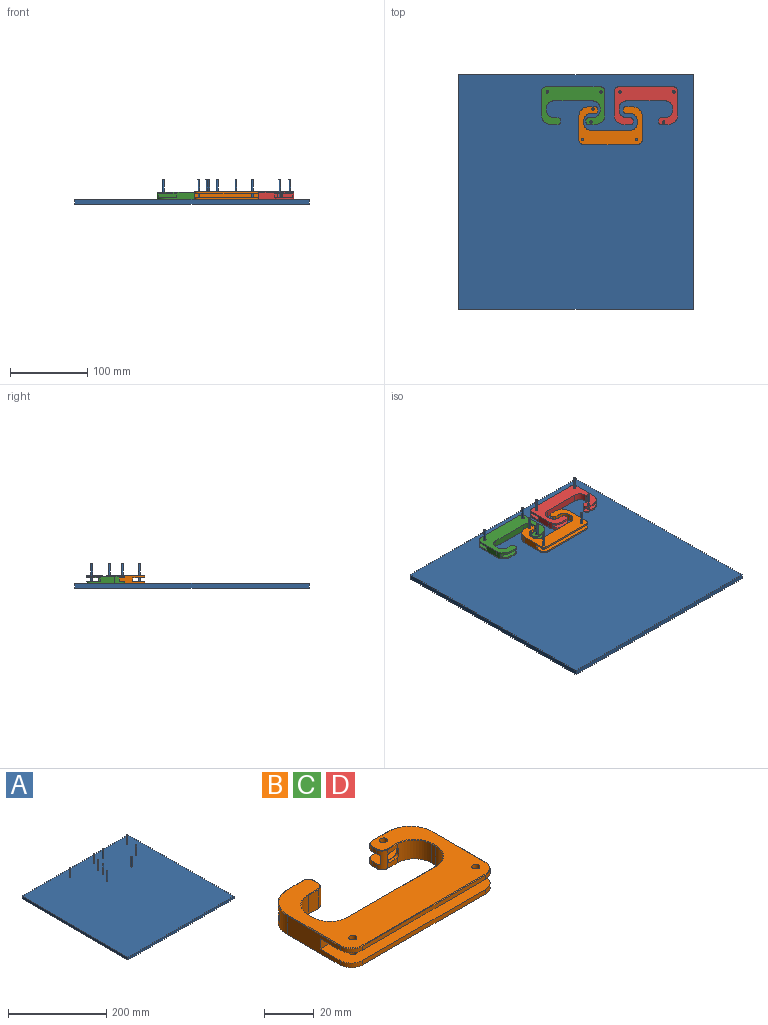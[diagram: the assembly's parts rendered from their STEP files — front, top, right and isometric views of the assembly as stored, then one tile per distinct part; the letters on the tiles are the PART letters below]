
ASSEMBLY  parts=4 mates=9
PART A: 24 faces, bbox 304.8x304.8x31.8 mm
  f0: plane 304.8x6.35mm, normal (1,0,0), area 1935.5mm2, adj f1,f3,f4,f5
  f1: plane 304.8x6.35mm, normal (0,1,0), area 1935.5mm2, adj f0,f2,f4,f5
  f2: plane 304.8x6.35mm, normal (-1,0,0), area 1935.5mm2, adj f1,f3,f4,f5
  f3: plane 304.8x6.35mm, normal (0,-1,0), area 1935.5mm2, adj f0,f2,f4,f5
  f4: plane 304.8x304.8mm, normal (0,0,1), area 92857.4mm2, adj f0,f1,f2,f3,f6,f8,f10,f12
  f5: plane 304.8x304.8mm, normal (0,0,-1), area 92903mm2, adj f0,f1,f2,f3
  f6: cylinder r=1.27mm len=25.4mm, axis (0,0,-1), area 202.7mm2, adj f4,f7
  f7: plane 2.54x2.54mm, normal (0,0,1), area 5.1mm2, adj f6
  f8: cylinder r=1.27mm len=25.4mm, axis (0,0,-1), area 202.7mm2, adj f4,f9
  f9: plane 2.54x2.54mm, normal (0,0,1), area 5.1mm2, adj f8
  f10: cylinder r=1.27mm len=25.4mm, axis (0,0,-1), area 202.7mm2, adj f4,f11
  f11: plane 2.54x2.54mm, normal (0,0,1), area 5.1mm2, adj f10
  f12: cylinder r=1.27mm len=25.4mm, axis (0,0,-1), area 202.7mm2, adj f4,f13
  f13: plane 2.54x2.54mm, normal (0,0,1), area 5.1mm2, adj f12
  f14: cylinder r=1.27mm len=25.4mm, axis (0,0,-1), area 202.7mm2, adj f4,f15
  f15: plane 2.54x2.54mm, normal (0,0,1), area 5.1mm2, adj f14
  f16: cylinder r=1.27mm len=25.4mm, axis (0,0,-1), area 202.7mm2, adj f4,f17
  f17: plane 2.54x2.54mm, normal (0,0,1), area 5.1mm2, adj f16
  f18: cylinder r=1.27mm len=25.4mm, axis (0,0,-1), area 202.7mm2, adj f4,f19
  f19: plane 2.54x2.54mm, normal (0,0,1), area 5.1mm2, adj f18
  f20: cylinder r=1.27mm len=25.4mm, axis (0,0,-1), area 202.7mm2, adj f4,f21
  f21: plane 2.54x2.54mm, normal (0,0,1), area 5.1mm2, adj f20
  f22: cylinder r=1.27mm len=25.4mm, axis (0,0,-1), area 202.7mm2, adj f4,f23
  f23: plane 2.54x2.54mm, normal (0,0,1), area 5.1mm2, adj f22
PART B: 87 faces, bbox 82.6x49.1x9.5 mm
  f0: plane 30.01x9.27mm, normal (-1,0,0), area 221.4mm2, adj f4,f17,f18,f42,f49,f73,f74,f86
  f1: plane 5.46x3.51mm, normal (0,-1,0), area 13.4mm2, adj f25,f27,f42,f76,f77,f78
  f2: plane 23.05x4.84mm, normal (0,1,0), area 82.7mm2, adj f21,f25,f46,f47,f75,f76,f77,f78
  f3: plane 69.85x2.24mm, normal (0,-1,0), area 156.6mm2, adj f18,f20,f42,f74
  f4: cylinder r=6.35mm len=6.35mm, axis (0,0,-1), area 19.8mm2, adj f0,f19,f51,f73
  f5: cylinder r=6.35mm len=6.35mm, axis (0,0,-1), area 19.8mm2, adj f6,f19,f55,f73
  f6: plane 30.01x9.27mm, normal (1,0,0), area 233.4mm2, adj f5,f20,f21,f42,f57,f72,f73,f74
  f7: cylinder r=1.63mm len=3.25mm, axis (0,0,-1), area 22.9mm2, adj f41,f73
  f8: cylinder r=1.63mm len=3.25mm, axis (0,0,-1), area 22.9mm2, adj f41,f73
  f9: plane 8.89x2.34mm, normal (0,1,0), area 20.8mm2, adj f15,f17,f42,f44
  f10: plane 8.89x2.09mm, normal (0,1,0), area 18.6mm2, adj f21,f23,f46,f61
  f11: cylinder r=3.17mm len=3.18mm, axis (0,0,-1), area 11.7mm2, adj f12,f22,f42,f47
  f12: plane 2.37x2.34mm, normal (-1,0,0), area 5.5mm2, adj f11,f25,f42,f47
  f13: plane 2.37x2.34mm, normal (1,0,0), area 5.5mm2, adj f15,f35,f42,f44
  f14: cylinder r=1.63mm len=3.25mm, axis (0,0,-1), area 23.9mm2, adj f42,f47
  f15: cylinder r=3.17mm len=3.18mm, axis (0,0,-1), area 11.7mm2, adj f9,f13,f42,f44
  f16: plane 8.89x2.09mm, normal (0,1,0), area 18.6mm2, adj f17,f39,f43,f50
  f17: cylinder r=12.7mm len=12.7mm, axis (0,0,-1), area 116.1mm2, adj f0,f9,f16,f42,f43,f44,f45,f48
  f18: cylinder r=6.35mm len=6.35mm, axis (0,0,-1), area 22.4mm2, adj f0,f3,f42,f74
  f19: plane 69.85x1.99mm, normal (0,-1,0), area 138.8mm2, adj f4,f5,f53,f73
  f20: cylinder r=6.35mm len=6.35mm, axis (0,0,-1), area 22.4mm2, adj f3,f6,f42,f74
  f21: cylinder r=12.7mm len=12.7mm, axis (0,0,-1), area 116.1mm2, adj f2,f6,f10,f22,f42,f46,f47,f59
  f22: plane 8.89x2.34mm, normal (0,1,0), area 20.8mm2, adj f11,f21,f42,f47
  f23: cylinder r=3.17mm len=3.18mm, axis (0,0,-1), area 10.4mm2, adj f10,f24,f46,f63
  f24: plane 2.37x2.09mm, normal (-1,0,0), area 4.9mm2, adj f23,f25,f46,f65
  f25: cylinder r=3.17mm len=9.27mm, axis (0,0,-1), area 37.8mm2, adj f1,f2,f12,f24,f26,f42,f46,f47
  f26: plane 5.46x3.26mm, normal (0,-1,0), area 12mm2, adj f25,f27,f69,f80,f81,f82
  f27: cylinder r=9.78mm len=9.78mm, axis (0,0,-1), area 138.9mm2, adj f1,f26,f28,f42,f71,f75,f76,f82
  f28: plane 9.27x2.37mm, normal (-1,0,0), area 22mm2, adj f27,f29,f42,f70
  f29: cylinder r=9.78mm len=9.78mm, axis (0,0,-1), area 142.4mm2, adj f28,f30,f42,f68
  f30: plane 50.29x9.27mm, normal (0,1,0), area 466.3mm2, adj f29,f31,f42,f66
  f31: cylinder r=9.78mm len=9.78mm, axis (0,0,-1), area 142.4mm2, adj f30,f32,f42,f64
  f32: plane 9.27x2.37mm, normal (1,0,0), area 22mm2, adj f31,f33,f42,f62
  f33: cylinder r=9.78mm len=9.78mm, axis (0,0,-1), area 142.4mm2, adj f32,f34,f42,f60
  f34: plane 9.27x5.46mm, normal (0,-1,0), area 50.6mm2, adj f33,f35,f42,f58
  f35: cylinder r=3.17mm len=9.27mm, axis (0,0,-1), area 38mm2, adj f13,f34,f36,f42,f43,f44,f45,f56
  f36: plane 2.37x2.09mm, normal (1,0,0), area 4.9mm2, adj f35,f39,f43,f54
  f37: cylinder r=1.63mm len=3.25mm, axis (0,0,-1), area 23.9mm2, adj f41,f46
  f38: cylinder r=1.63mm len=3.25mm, axis (0,0,-1), area 22.9mm2, adj f42,f74
  f39: cylinder r=3.17mm len=3.18mm, axis (0,0,-1), area 10.4mm2, adj f16,f36,f43,f52
  f40: cylinder r=1.63mm len=3.25mm, axis (0,0,-1), area 22.9mm2, adj f42,f74
  f41: plane 82.04x48.55mm, normal (0,0,1), area 2101.3mm2, adj f7,f8,f37,f48,f49,f50,f51,f52
  f42: plane 82.55x49.06mm, normal (0,0,-1), area 2192.5mm2, adj f0,f1,f3,f6,f9,f11,f12,f13
  f43: plane 23.5x7.17mm, normal (0,0,-1), area 142.8mm2, adj f16,f17,f35,f36,f39,f45
  f44: plane 23.5x7.17mm, normal (0,0,1), area 142.8mm2, adj f9,f13,f15,f17,f35,f45
  f45: plane 23.05x4.84mm, normal (0,1,0), area 111.5mm2, adj f17,f35,f43,f44
  f46: plane 23.5x7.17mm, normal (0,0,-1), area 134.5mm2, adj f2,f10,f21,f23,f24,f25,f37
  f47: plane 23.5x7.17mm, normal (0,0,1), area 134.5mm2, adj f2,f11,f12,f14,f21,f22,f25
  f48: cone r=12.45mm half-angle=45deg, axis (0,0,-1), area 7.1mm2, adj f17,f41,f49,f50
  f49: plane 30.01x0.25mm, normal (-0.71,0,0.71), area 10.8mm2, adj f0,f41,f48,f51
  f50: plane 8.89x0.25mm, normal (0,0.71,0.71), area 3.2mm2, adj f16,f41,f48,f52
  f51: cone r=6.1mm half-angle=45deg, axis (0,0,-1), area 3.5mm2, adj f4,f41,f49,f53
  f52: cone r=2.92mm half-angle=45deg, axis (0,0,-1), area 1.7mm2, adj f39,f41,f50,f54
  f53: plane 69.85x0.25mm, normal (0,-0.71,0.71), area 25.1mm2, adj f19,f41,f51,f55
  f54: plane 2.37x0.25mm, normal (0.71,0,0.71), area 0.9mm2, adj f36,f41,f52,f56
  f55: cone r=6.1mm half-angle=45deg, axis (0,0,-1), area 3.5mm2, adj f5,f41,f53,f57
  f56: cone r=2.92mm half-angle=45deg, axis (0,0,-1), area 1.7mm2, adj f35,f41,f54,f58
  f57: plane 30.01x0.25mm, normal (0.71,0,0.71), area 10.8mm2, adj f6,f41,f55,f59
  f58: plane 5.46x0.25mm, normal (0,-0.71,0.71), area 2mm2, adj f34,f41,f56,f60
  f59: cone r=12.45mm half-angle=45deg, axis (0,0,-1), area 7.1mm2, adj f21,f41,f57,f61
  f60: cone r=9.78mm half-angle=45deg, axis (0,0,1), area 5.6mm2, adj f33,f41,f58,f62
  f61: plane 8.89x0.25mm, normal (0,0.71,0.71), area 3.2mm2, adj f10,f41,f59,f63
  f62: plane 2.37x0.25mm, normal (0.71,0,0.71), area 0.9mm2, adj f32,f41,f60,f64
  f63: cone r=2.92mm half-angle=45deg, axis (0,0,-1), area 1.7mm2, adj f23,f41,f61,f65
  f64: cone r=9.78mm half-angle=45deg, axis (0,0,1), area 5.6mm2, adj f31,f41,f62,f66
  f65: plane 2.37x0.25mm, normal (-0.71,0,0.71), area 0.9mm2, adj f24,f41,f63,f67
  f66: plane 50.29x0.25mm, normal (0,0.71,0.71), area 18.1mm2, adj f30,f41,f64,f68
  f67: cone r=3.17mm half-angle=45deg, axis (0,0,-1), area 1.7mm2, adj f25,f41,f65,f69
  f68: cone r=10.03mm half-angle=45deg, axis (0,0,1), area 5.6mm2, adj f29,f41,f66,f70
  f69: plane 5.46x0.25mm, normal (0,-0.71,0.71), area 2mm2, adj f26,f41,f67,f71
  f70: plane 2.37x0.25mm, normal (-0.71,0,0.71), area 0.9mm2, adj f28,f41,f68,f71
  f71: cone r=10.03mm half-angle=45deg, axis (0,0,1), area 5.6mm2, adj f27,f41,f69,f70
  f72: plane 77.53x5.04mm, normal (0,-1,0), area 384mm2, adj f6,f73,f74,f83,f84,f85
  f73: plane 82.55x17.62mm, normal (0,0,-1), area 1236.1mm2, adj f0,f4,f5,f6,f7,f8,f19,f72
  f74: plane 82.55x17.62mm, normal (0,0,1), area 1236.1mm2, adj f0,f3,f6,f18,f20,f38,f40,f72
  f75: plane 1.61x1.6mm, normal (-1,0,0), area 2.6mm2, adj f2,f27,f76,f82
  f76: cylinder r=1.59mm len=1.6mm, axis (0,1,0), area 3.9mm2, adj f1,f2,f27,f75,f77
  f77: plane 3.3x1.55mm, normal (0,0,1), area 5.1mm2, adj f1,f2,f76,f78
  f78: cylinder r=1.59mm len=1.59mm, axis (0,1,0), area 3.9mm2, adj f1,f2,f25,f77,f79
  f79: plane 1.61x1.55mm, normal (1,0,0), area 2.5mm2, adj f2,f25,f78,f80
  f80: cylinder r=1.59mm len=1.59mm, axis (0,1,0), area 3.9mm2, adj f2,f25,f26,f79,f81
  f81: plane 3.3x1.55mm, normal (0,0,-1), area 5.1mm2, adj f2,f26,f80,f82
  f82: cylinder r=1.59mm len=1.6mm, axis (0,1,0), area 3.9mm2, adj f2,f26,f27,f75,f81
  f83: plane 2.38x1.87mm, normal (-1,0,0), area 4.4mm2, adj f72,f84,f85,f86
  f84: cylinder r=1.59mm len=2.38mm, axis (0,-1,0), area 5.9mm2, adj f72,f73,f83,f86
  f85: cylinder r=1.59mm len=2.38mm, axis (0,-1,0), area 5.9mm2, adj f72,f74,f83,f86
  f86: plane 6.6x5.04mm, normal (0,-1,0), area 32.2mm2, adj f0,f73,f74,f83,f84,f85
PART C: same geometry as B
PART D: same geometry as B
PLACE A t=(-0.79,-0.33,-15.69)mm fixed
PLACE B rot(axis=(0,1,0),180deg) t=(44.07,96.23,-4.57)mm
PLACE C rot(axis=(1,0,0),180deg) t=(-4.42,101.32,-4.57)mm
PLACE D rot(axis=(-1,0,0),180deg) t=(90.02,101.32,-4.57)mm
MATE parallel B.f19 <-> A.f3  axis (0,-1,0) through (44.07,61.26,-8.09)mm
MATE revolute C.f14 <-> A.f18  axis (0,0,1) through (18.44,90.41,-9.34)mm
MATE parallel C.f16 <-> A.f3  axis (0,-1,0) through (-28.55,87.23,-8.04)mm
MATE parallel A.f4 <-> C.f41  axis (0,0,1) through (-0.81,-0.38,-9.34)mm
MATE revolute B.f7 <-> A.f16  axis (0,0,1) through (77.72,67.93,-9.34)mm
MATE planar A.f4 <-> B.f41  axis (0,0,1) through (-0.81,-0.38,-9.34)mm
MATE revolute D.f14 <-> A.f8  axis (0,0,1) through (112.88,90.41,-9.34)mm
MATE parallel D.f9 <-> A.f3  axis (0,-1,0) through (65.89,87.23,-0.98)mm
MATE planar A.f4 <-> D.f41  axis (0,0,1) through (-0.81,-0.38,-9.34)mm
